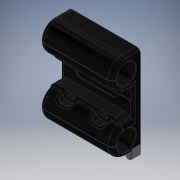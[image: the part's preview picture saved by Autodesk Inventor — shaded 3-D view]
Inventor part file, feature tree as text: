
AUTODESK INVENTOR PART (.ipt)
format: ipt  version: 2018 (Build 220112000, 112)  size: 433,152 bytes
history: native  units: mm
features: extrude x1, fillet x1, sketch x1
ambient origin geometry x8: Origin, YZ Plane, XZ Plane, XY Plane, X Axis, Y Axis, Z Axis, Center Point
bodies: Solid1 (feature_tree), Solid2 (feature_tree)
feature tree (3):
  extrude  "Extrusion1"  TaperAngle=30.0deg  [1 undecoded]
  fillet  "Fillet1"  Radius=8.0mm
  sketch  "Sketch1"  dims[d1=6.5mm d2=30.0deg d3=8.0mm d4=0.0mm d5=2.0mm]
note: 1 required parameter value undecoded (feature->parameter linkage not recoverable at this tier; creation-order binding heuristic only, values carry confidence <= 0.55)
